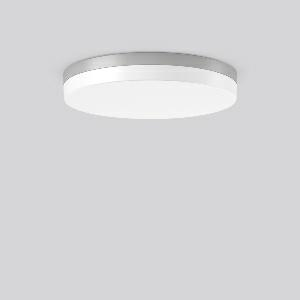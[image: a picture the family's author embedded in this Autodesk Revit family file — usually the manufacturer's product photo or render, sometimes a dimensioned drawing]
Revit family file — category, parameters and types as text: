
# Revit family: flat_slim_round_312634_004_1_730_5408
name_source: partatom
category: Lighting Fixtures
units: mm (PartAtom-declared; Revit-internal decimal feet)

## family parameters
Cut with Voids When Loaded = No
Host = Face
Light Source = No
Part Type = Normal
Room Calculation Point = No
Round Connector Dimension = Use Diameter
Shared = No

## types (1)
- MultiLumen 1 830 (1 x LED Modul 830, 3500 lm, 3000)
    Apparent Load = 24 VA
    CIE Flux Codes = 38 68 89 85 100
    Color Rendering = 80
    Color Temperature = 3000
    Default Elevation = 1800 mm
    Height = 70 mm
    Lamp = 1 x LED Modul 830
    Lamp Light Flux = 3500 lm
    Lamp count = 1
    Length = 480 mm
    Lifetime = 50000 h
    Luminous efficacy = 146 lm/W
    Manufacturer = RZB
    ModVariant = No
    Model = 312634.004.1.730
    Mounting Place = Ceiling
    Mounting Type = Surface mounted
    Number of Poles = 1
    OnlyDefault = Yes
    Power Factor = 1
    Product Name = FLAT SLIM round
    Product group = Surface mounted ceiling and wall luminaires
    ProductGroupID = 305
    Protection Class = Protection class I
    Protection Degree = Degree of protection
    RLX_Detail_Level = 1
    RLX_Emergency_Light_Flux = 0 lm
    RLX_Emergency_Type = 0
    RLX_Emergency_Type_DB = No
    RlxData = <blob elided: 22105 chars, md5=4f9b9ed8>
    Socket = socket
    Standby Power = 0 W
    System Light Flux = 3500 lm
    System Power = 24 W
    Type Comments = MultiLumen 1 830
    Type Image = 312633.004.jpg
    URL = http://relux.com
    VarID = multilumen_1_830
    Voltage = 0 V
    Weight = 0.00 kg
    Width = 0 mm  [stored 0 ft]

note: [stored X ft] marks values corroborated as IEEE doubles in the binary element streams (Revit-internal decimal feet)

## geometry (parser evidence)
native form markers: Blend x4, Sweep x16
no freeform markers — native parametric forms only
